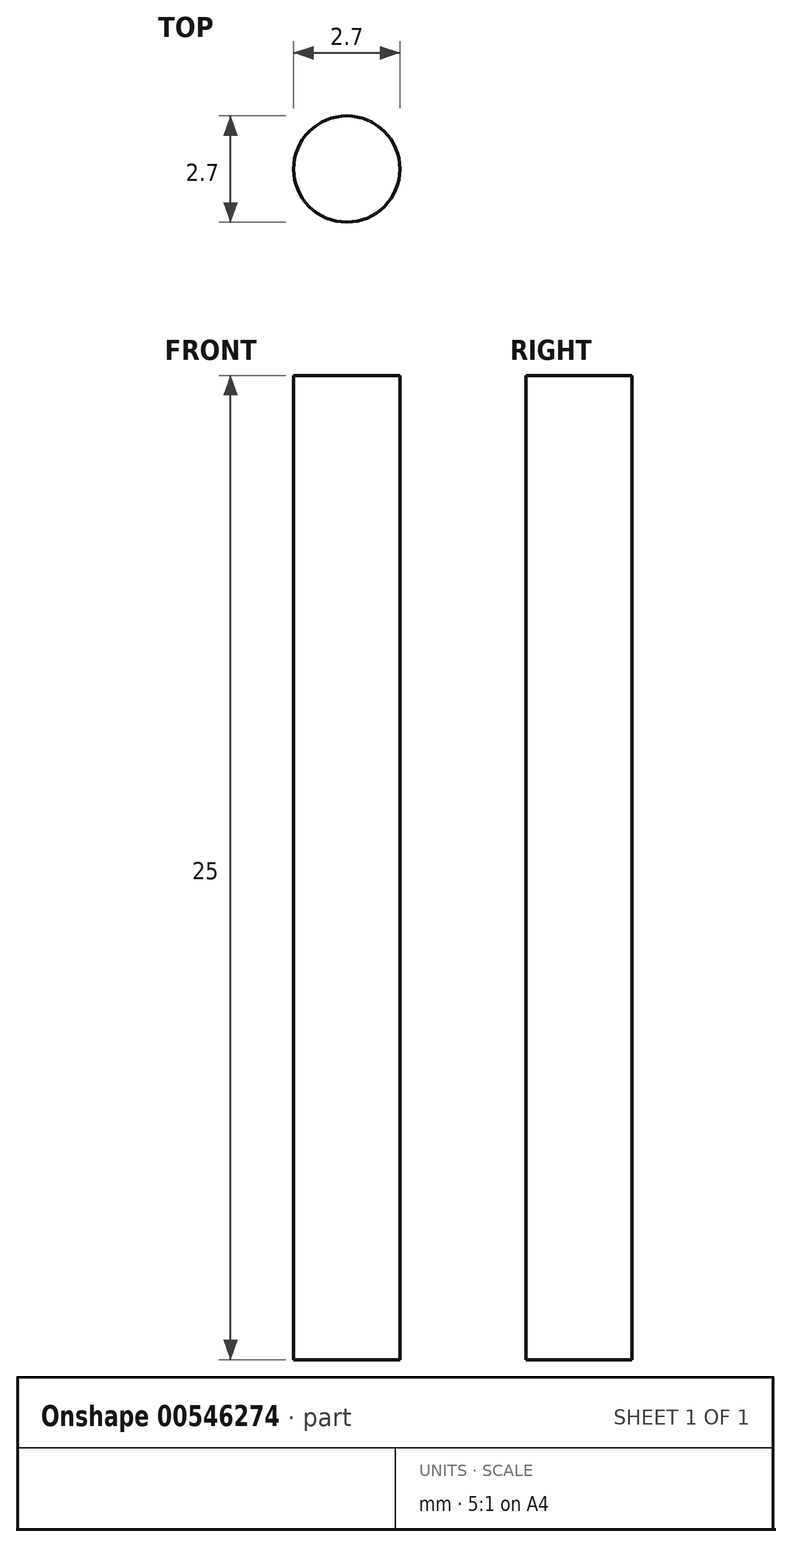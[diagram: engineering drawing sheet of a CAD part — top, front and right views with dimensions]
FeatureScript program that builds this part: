
annotation { "Feature Type Name" : "Feature", "Feature Type Description" : "" }
export const myFeature = defineFeature(function(context is Context, id is Id, definition is map)
    precondition{}
    {
        {
            var Q0;
            Q0=qCreatedBy(makeId("Top.planeOp"),FACE);
            var sketch = newSketch(context, id + "F0", { "sketchPlane" : qUnion([Q0])});
            skCircle(sketch, "E0", {"center": v(0, 0) * mm, "radius": 1.35 * mm});
            skSolve(sketch);
        }
        {
            var Q0;
            Q0 = qSketchRegion(id + "F0", true);
            extrude(context, id + "F1", {"entities" : qUnion([Q0]), "depth" : 25 * mm, "offsetDistance" : 25 * mm});
        }
    });
